# Revit family: Window_Shade-Draper_Inc.-Motor_Dual _Roller_FlexShade
name_source: partatom
category: Specialty Equipment
revit_build: Autodesk Revit 2017 (Build: 20160225_1515(x64)
units: mm (PartAtom-declared; Revit-internal decimal feet)

## family parameters
Always vertical = Yes
Cut with Voids When Loaded = No
OmniClass Number = 23.30.20.11
OmniClass Title = Window Components
Part Type = Normal
Room Calculation Point = No
Round Connector Dimension = Use Diameter
Shared = No
Work Plane-Based = No

## types (1)
- Dual Roller Motorized FlexShade
    A = 4 5/8"
    Apparent Load = 156 VA
    B = 6 13/16"
    Brackets Only = Yes
    C = 0"
    C Height = 6' - 0"
    C Length = 4' - 0"
    D = 0"
    Depth = 4 5/8"
    Description = Dual Shade
    E = 1"
    Fascia = No
    Fascia Material = Powder Coat - Draper - White
    Frequency = 60 Hz
    Head Box = No
    Length = 4' - 0"
    Manufacturer = Draper Inc.
    Model = Dual Roller FlexShade
    Number of Poles = 1
    Overall Height = 6' - 0"
    Phase = 1
    Power Factor = 1
    Product Documentation Link = https://www.draperinc.com
    Product Name = Dual Roller FlexShade
    Product Page URL = https://www.draperinc.com
    Shade Material = Fabric - Draper - Green Screen Revive 5%
    URL = http://www.DraperInc.com
    Voltage = 120 V
    Width = 6 13/16"

## geometry (parser evidence)
native form markers: Blend x6, Sweep x13
no freeform markers — native parametric forms only
